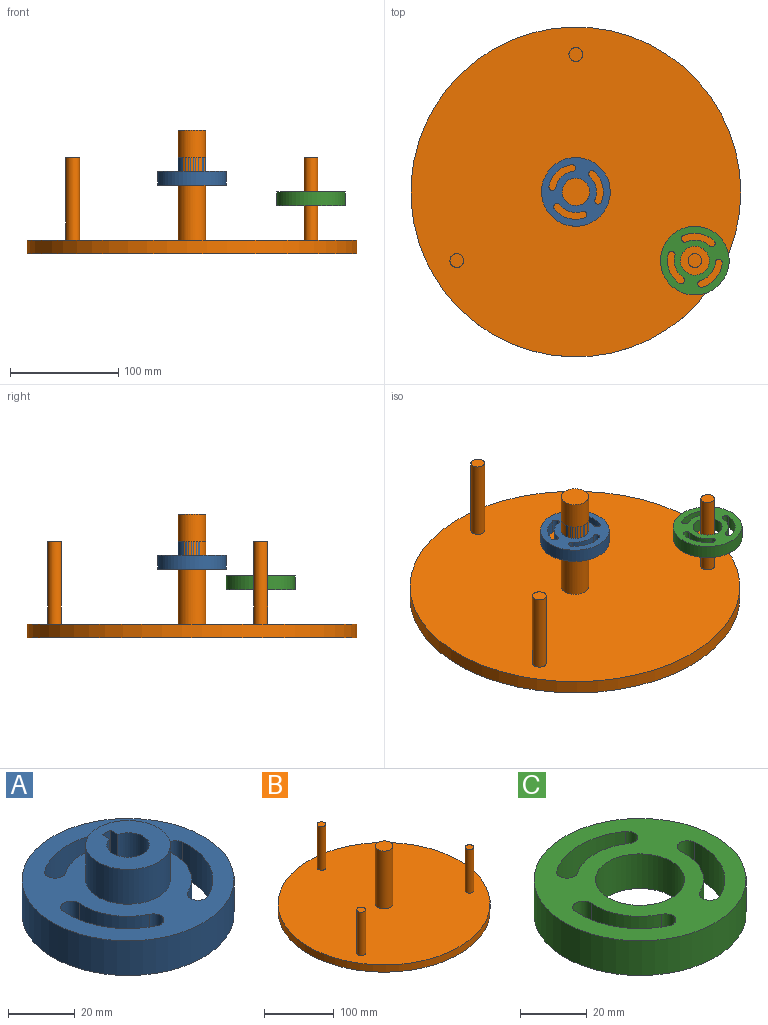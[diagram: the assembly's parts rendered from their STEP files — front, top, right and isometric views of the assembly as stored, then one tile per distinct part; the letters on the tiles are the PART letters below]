
ASSEMBLY  parts=3 mates=2
PART A: 21 faces, bbox 63.5x63.5x25.4 mm
  f0: plane 25.4x3.18mm, normal (1,0,0), area 80.6mm2, adj f1,f3,f5,f6
  f1: plane 25.4x3.43mm, normal (0,-1,0), area 87.1mm2, adj f0,f2,f5,f6
  f2: plane 25.4x3.18mm, normal (-1,0,0), area 80.6mm2, adj f1,f3,f5,f6
  f3: cylinder r=6.35mm len=25.4mm, axis (0,0,-1), area 925.2mm2, adj f0,f2,f5,f6
  f4: cylinder r=12.7mm len=25.4mm, axis (0,0,-1), area 1013.4mm2, adj f5,f8
  f5: plane 25.4x25.4mm, normal (0,0,1), area 369.7mm2, adj f0,f1,f2,f3,f4
  f6: plane 63.5x63.5mm, normal (0,0,-1), area 2419.8mm2, adj f0,f1,f2,f3,f7,f9,f10,f11
  f7: cylinder r=31.75mm len=63.5mm, axis (0,0,-1), area 2533.5mm2, adj f6,f8
  f8: plane 63.5x63.5mm, normal (0,0,1), area 2050.2mm2, adj f4,f7,f9,f10,f11,f12,f13,f14
  f9: cylinder r=3.17mm len=12.7mm, axis (0,0,1), area 126.7mm2, adj f6,f8,f10,f12
  f10: cylinder r=25.4mm len=25.14mm, axis (0,0,1), area 392.4mm2, adj f6,f8,f9,f11
  f11: cylinder r=3.17mm len=12.7mm, axis (0,0,1), area 126.7mm2, adj f6,f8,f10,f12
  f12: cylinder r=19.05mm len=18.85mm, axis (0,0,1), area 294.3mm2, adj f6,f8,f9,f11
  f13: cylinder r=3.17mm len=12.7mm, axis (0,0,1), area 126.7mm2, adj f6,f8,f14,f16
  f14: cylinder r=25.4mm len=25.14mm, axis (0,0,1), area 392.4mm2, adj f6,f8,f13,f15
  f15: cylinder r=3.17mm len=12.7mm, axis (0,0,1), area 126.7mm2, adj f6,f8,f14,f16
  f16: cylinder r=19.05mm len=18.85mm, axis (0,0,1), area 294.3mm2, adj f6,f8,f13,f15
  f17: cylinder r=3.17mm len=12.7mm, axis (0,0,1), area 126.7mm2, adj f6,f8,f18,f20
  f18: cylinder r=25.4mm len=29.03mm, axis (0,0,1), area 392.4mm2, adj f6,f8,f17,f19
  f19: cylinder r=3.17mm len=12.7mm, axis (0,0,1), area 126.7mm2, adj f6,f8,f18,f20
  f20: cylinder r=19.05mm len=21.77mm, axis (0,0,1), area 294.3mm2, adj f6,f8,f17,f19
PART B: 11 faces, bbox 304.8x304.8x114.3 mm
  f0: cylinder r=152.4mm len=304.8mm, axis (0,0,-1), area 12161mm2, adj f1,f2
  f1: plane 304.8x304.8mm, normal (0,0,1), area 72079.1mm2, adj f0,f3,f5,f8,f9
  f2: plane 304.8x304.8mm, normal (0,0,-1), area 72965.9mm2, adj f0
  f3: cylinder r=12.7mm len=101.6mm, axis (0,0,-1), area 8107.3mm2, adj f1,f4
  f4: plane 25.4x25.4mm, normal (0,0,1), area 506.7mm2, adj f3
  f5: cylinder r=6.35mm len=76.2mm, axis (0,0,-1), area 3040.2mm2, adj f1,f6
  f6: plane 12.7x12.7mm, normal (0,0,1), area 126.7mm2, adj f5
  f7: plane 12.7x12.7mm, normal (0,0,1), area 126.7mm2, adj f8
  f8: cylinder r=6.35mm len=76.2mm, axis (0,0,-1), area 3040.2mm2, adj f1,f7
  f9: cylinder r=6.35mm len=76.2mm, axis (0,0,-1), area 3040.2mm2, adj f1,f10
  f10: plane 12.7x12.7mm, normal (0,0,1), area 126.7mm2, adj f9
PART C: 16 faces, bbox 63.5x63.5x12.7 mm
  f0: cylinder r=25.4mm len=29.03mm, axis (0,0,-1), area 392.4mm2, adj f1,f9,f13,f14
  f1: cylinder r=3.17mm len=12.7mm, axis (0,0,-1), area 126.7mm2, adj f0,f2,f13,f14
  f2: cylinder r=19.05mm len=21.77mm, axis (0,0,-1), area 294.3mm2, adj f1,f9,f13,f14
  f3: cylinder r=19.05mm len=18.85mm, axis (0,0,-1), area 294.3mm2, adj f4,f10,f13,f14
  f4: cylinder r=3.17mm len=12.7mm, axis (0,0,-1), area 126.7mm2, adj f3,f5,f13,f14
  f5: cylinder r=25.4mm len=25.14mm, axis (0,0,-1), area 392.4mm2, adj f4,f10,f13,f14
  f6: cylinder r=19.05mm len=18.85mm, axis (0,0,-1), area 294.3mm2, adj f7,f11,f13,f14
  f7: cylinder r=3.17mm len=12.7mm, axis (0,0,-1), area 126.7mm2, adj f6,f8,f13,f14
  f8: cylinder r=25.4mm len=25.14mm, axis (0,0,-1), area 392.4mm2, adj f7,f11,f13,f14
  f9: cylinder r=3.17mm len=12.7mm, axis (0,0,-1), area 126.7mm2, adj f0,f2,f13,f14
  f10: cylinder r=3.17mm len=12.7mm, axis (0,0,-1), area 126.7mm2, adj f3,f5,f13,f14
  f11: cylinder r=3.17mm len=12.7mm, axis (0,0,-1), area 126.7mm2, adj f6,f8,f13,f14
  f12: cylinder r=31.75mm len=63.5mm, axis (0,0,-1), area 2533.5mm2, adj f13,f14
  f13: plane 63.5x63.5mm, normal (0,0,1), area 1998.2mm2, adj f0,f1,f2,f3,f4,f5,f6,f7
  f14: plane 63.5x63.5mm, normal (0,0,-1), area 1998.2mm2, adj f0,f1,f2,f3,f4,f5,f6,f7
  f15: cylinder r=13.33mm len=26.67mm, axis (0,0,1), area 1064.1mm2, adj f13,f14
PLACE A rot(axis=(0,0,1),163.3deg) t=(0,0,50.8)mm
PLACE B t=(0,0,-12.7)mm
PLACE C rot(axis=(0,0,-1),129.8deg) t=(109.99,-63.5,31.75)mm
MATE revolute A.f3 <-> B.f0  axis (0,0,-1) through (0,0,50.8)mm
MATE revolute C.f0 <-> B.f8  axis (0,0,-1) through (109.99,-63.5,38.1)mm
